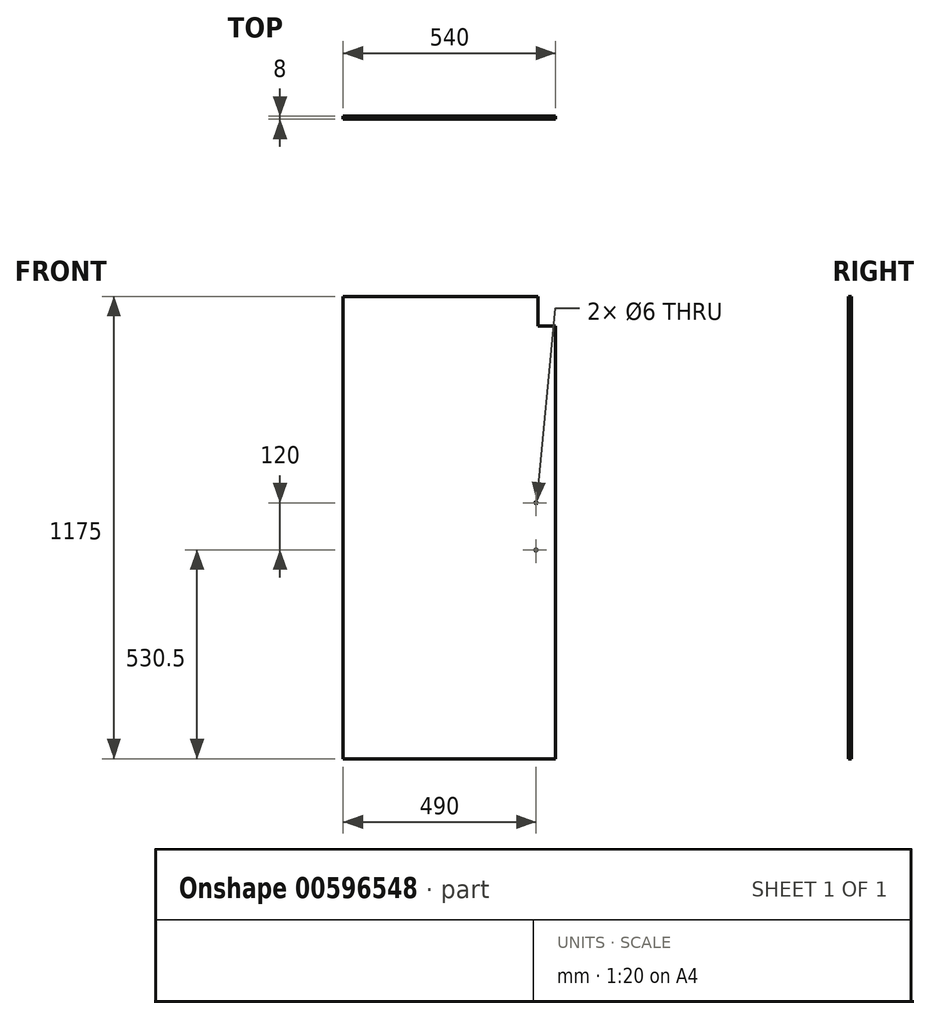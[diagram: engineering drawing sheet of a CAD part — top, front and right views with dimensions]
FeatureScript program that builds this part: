
annotation { "Feature Type Name" : "Feature", "Feature Type Description" : "" }
export const myFeature = defineFeature(function(context is Context, id is Id, definition is map)
    precondition{}
    {
        {
            var Q0;
            Q0=qCreatedBy(makeId("Front.planeOp"),FACE);
            var sketch = newSketch(context, id + "F0", { "sketchPlane" : qUnion([Q0])});
            skLineSegment(sketch, "E0.bottom", {"start": v(0, 0) * mm, "end": v(540, 0) * mm});
            skLineSegment(sketch, "E0.top", {"start": v(0, 1175) * mm, "end": v(495, 1175) * mm});
            skLineSegment(sketch, "E0.left", {"start": v(0, 0) * mm, "end": v(0, 1175) * mm});
            skLineSegment(sketch, "E1.0", {"start": v(540, 0) * mm, "end": v(540, 1100) * mm});
            skLineSegment(sketch, "E2.0", {"start": v(495, 1100) * mm, "end": v(495, 1175) * mm});
            skLineSegment(sketch, "E3.0", {"start": v(495, 1100) * mm, "end": v(540, 1100) * mm});
            skCircle(sketch, "E4", {"center": v(490, 530.5) * mm, "radius": 3 * mm});
            skCircle(sketch, "E5", {"center": v(490, 650.5) * mm, "radius": 3 * mm});
            skSolve(sketch);
        }
        {
            var Q0;
            Q0 = qSketchRegion(id + "F0", true);
            extrude(context, id + "F1", {"entities" : qUnion([Q0]), "depth" : 8 * mm, "offsetDistance" : 25 * mm});
        }
    });
